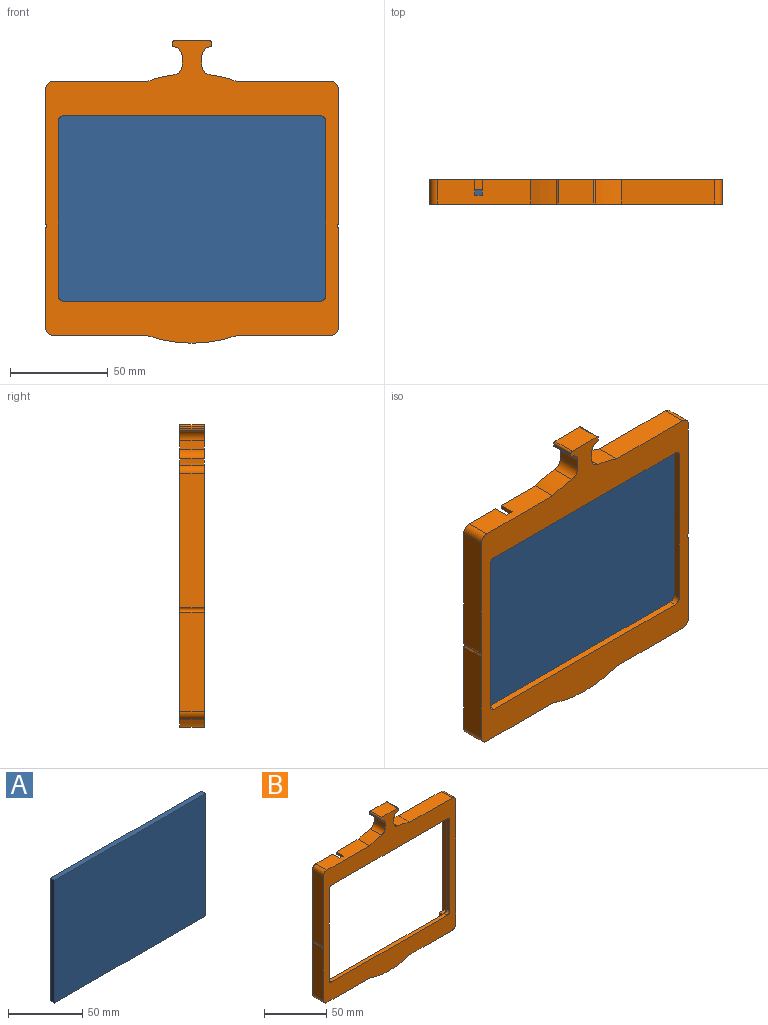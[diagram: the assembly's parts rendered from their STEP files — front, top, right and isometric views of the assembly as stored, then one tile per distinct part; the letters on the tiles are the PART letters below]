
ASSEMBLY  parts=2 mates=1
PART A: 6 faces, bbox 144x3.9x101.3 mm
  f0: plane 144x3.9mm, normal (0,0,1), area 561.6mm2, adj f1,f3,f4,f5
  f1: plane 101.3x3.9mm, normal (-1,0,0), area 395.1mm2, adj f0,f2,f4,f5
  f2: plane 144x3.9mm, normal (0,0,-1), area 561.6mm2, adj f1,f3,f4,f5
  f3: plane 101.3x3.9mm, normal (1,0,0), area 395.1mm2, adj f0,f2,f4,f5
  f4: plane 144x101.3mm, normal (0,-1,0), area 14587.2mm2, adj f0,f1,f2,f3
  f5: plane 144x101.3mm, normal (0,1,0), area 14587.2mm2, adj f0,f1,f2,f3
PART B: 106 faces, bbox 149.8x12.6x154.8 mm
  f0: plane 48.63x10mm, normal (0,0,1), area 486.3mm2, adj f1,f3,f51,f91,f95
  f1: plane 145.84x126mm, normal (0,1,0), area 3155mm2, adj f0,f2,f5,f6,f8,f10,f11,f50
  f2: plane 48.63x10mm, normal (0,0,-1), area 454.3mm2, adj f1,f3,f52,f85,f86,f87,f89,f94
  f3: plane 154.82x149.84mm, normal (0,1,0), area 1353.4mm2, adj f0,f2,f4,f5,f6,f7,f8,f9
  f4: plane 47.77x12.56mm, normal (0,0,1), area 568mm2, adj f3,f20,f33,f46,f85,f86,f87
  f5: plane 120x10mm, normal (-1,0,0), area 980.7mm2, adj f1,f3,f7,f9,f54,f55,f56,f58
  f6: plane 48.63x10mm, normal (0,0,1), area 430.3mm2, adj f1,f3,f7,f78,f80,f91,f96
  f7: cylinder r=3mm len=3mm, axis (0,-1,0), area 9.4mm2, adj f3,f5,f6,f78
  f8: plane 48.63x10mm, normal (0,0,-1), area 430.3mm2, adj f1,f3,f9,f71,f73,f89,f92
  f9: cylinder r=3mm len=3mm, axis (0,1,0), area 9.4mm2, adj f3,f5,f8,f71
  f10: plane 130.92x1mm, normal (0,0,1), area 130.9mm2, adj f1,f54,f57,f69
  f11: plane 130.92x1mm, normal (0,0,-1), area 130.9mm2, adj f1,f54,f61,f64
  f12: plane 131x3.56mm, normal (0,0,-1), area 466.4mm2, adj f16,f17,f20,f54
  f13: plane 89x3.56mm, normal (1,0,0), area 316.8mm2, adj f17,f18,f20,f54
  f14: plane 89x3.56mm, normal (-1,0,0), area 316.8mm2, adj f16,f19,f20,f54
  f15: plane 131x3.56mm, normal (0,0,1), area 466.4mm2, adj f18,f19,f20,f54
  f16: cylinder r=3mm len=3.56mm, axis (0,1,0), area 16.8mm2, adj f12,f14,f20,f54
  f17: cylinder r=3mm len=3.56mm, axis (0,-1,0), area 16.8mm2, adj f12,f13,f20,f54
  f18: cylinder r=3mm len=3.56mm, axis (0,1,0), area 16.8mm2, adj f13,f15,f20,f54
  f19: cylinder r=3mm len=3.56mm, axis (0,-1,0), area 16.8mm2, adj f14,f15,f20,f54
  f20: plane 154.82x149.84mm, normal (0,-1,0), area 6922mm2, adj f4,f12,f13,f14,f15,f16,f17,f18
  f21: plane 50.88x12.56mm, normal (-1,0,0), area 639.1mm2, adj f3,f20,f47,f49
  f22: plane 68.88x12.56mm, normal (1,0,0), area 865.2mm2, adj f3,f20,f45,f48
  f23: plane 50.88x12.56mm, normal (1,0,0), area 639.1mm2, adj f3,f20,f44,f48
  f24: plane 47.77x12.56mm, normal (0,0,1), area 600mm2, adj f3,f20,f25,f45
  f25: cylinder r=69mm len=13.83mm, axis (0,1,0), area 179.1mm2, adj f3,f20,f24,f42
  f26: plane 12.56x4.5mm, normal (1,0,0), area 56.5mm2, adj f3,f20,f27,f42
  f27: cylinder r=5mm len=12.56mm, axis (0,1,0), area 88.1mm2, adj f3,f20,f26,f38
  f28: plane 12.56x1.08mm, normal (1,0,0), area 13.6mm2, adj f3,f20,f38,f39
  f29: plane 18x12.56mm, normal (0,0,1), area 226.1mm2, adj f3,f20,f39,f40
  f30: plane 12.56x1.08mm, normal (-1,0,0), area 13.6mm2, adj f3,f20,f40,f41
  f31: cylinder r=5mm len=12.56mm, axis (0,1,0), area 88.1mm2, adj f3,f20,f32,f41
  f32: plane 12.56x4.5mm, normal (-1,0,0), area 56.5mm2, adj f3,f20,f31,f43
  f33: cylinder r=69mm len=13.83mm, axis (0,1,0), area 179.1mm2, adj f3,f4,f20,f43
  f34: plane 68.88x12.56mm, normal (-1,0,0), area 865.2mm2, adj f3,f20,f46,f49
  f35: plane 47.77x12.56mm, normal (0,0,-1), area 600mm2, adj f3,f20,f36,f47
  f36: cylinder r=69mm len=46.3mm, axis (0,1,0), area 593.1mm2, adj f3,f20,f35,f37
  f37: plane 47.77x12.56mm, normal (0,0,-1), area 600mm2, adj f3,f20,f36,f44
  f38: cylinder r=1mm len=12.56mm, axis (0,1,0), area 17.6mm2, adj f3,f20,f27,f28
  f39: cylinder r=1mm len=12.56mm, axis (0,1,0), area 19.7mm2, adj f3,f20,f28,f29
  f40: cylinder r=1mm len=12.56mm, axis (0,1,0), area 19.7mm2, adj f3,f20,f29,f30
  f41: cylinder r=1mm len=12.56mm, axis (0,1,0), area 17.6mm2, adj f3,f20,f30,f31
  f42: cylinder r=5mm len=12.56mm, axis (0,1,0), area 90.1mm2, adj f3,f20,f25,f26
  f43: cylinder r=5mm len=12.56mm, axis (0,1,0), area 90.1mm2, adj f3,f20,f32,f33
  f44: cylinder r=4mm len=12.56mm, axis (0,1,0), area 78.9mm2, adj f3,f20,f23,f37
  f45: cylinder r=4mm len=12.56mm, axis (0,1,0), area 78.9mm2, adj f3,f20,f22,f24
  f46: cylinder r=4mm len=12.56mm, axis (0,1,0), area 78.9mm2, adj f3,f4,f20,f34
  f47: cylinder r=4mm len=12.56mm, axis (0,1,0), area 78.9mm2, adj f3,f20,f21,f35
  f48: cylinder r=1.5mm len=12.56mm, axis (0,1,0), area 31.7mm2, adj f3,f20,f22,f23
  f49: cylinder r=1.5mm len=12.56mm, axis (0,1,0), area 31.7mm2, adj f3,f20,f21,f34
  f50: plane 120x10mm, normal (1,0,0), area 1200mm2, adj f1,f3,f51,f52
  f51: cylinder r=3mm len=10mm, axis (0,1,0), area 47.1mm2, adj f0,f1,f3,f50
  f52: cylinder r=3mm len=10mm, axis (0,-1,0), area 47.1mm2, adj f1,f2,f3,f50
  f53: plane 117.3x8mm, normal (-1,0,0), area 226.5mm2, adj f1,f54,f63,f66,f67,f70,f76,f84
  f54: plane 142.92x101.7mm, normal (0,1,0), area 1527.7mm2, adj f5,f10,f11,f12,f13,f14,f15,f16
  f55: plane 7x6mm, normal (0,0,-1), area 42mm2, adj f5,f54,f57,f58
  f56: plane 8x6mm, normal (0,0,1), area 48mm2, adj f1,f5,f57,f58
  f57: plane 8x3mm, normal (-1,0,0), area 24mm2, adj f1,f10,f55,f56,f58
  f58: plane 6x3mm, normal (0,1,0), area 18mm2, adj f5,f55,f56,f57
  f59: plane 7x6mm, normal (0,0,1), area 42mm2, adj f5,f54,f61,f62
  f60: plane 8x6mm, normal (0,0,-1), area 48mm2, adj f1,f5,f61,f62
  f61: plane 8x3mm, normal (-1,0,0), area 24mm2, adj f1,f11,f59,f60,f62
  f62: plane 6x3mm, normal (0,1,0), area 18mm2, adj f5,f59,f60,f61
  f63: plane 7x6mm, normal (0,0,1), area 42mm2, adj f53,f54,f64,f66
  f64: plane 8x3mm, normal (1,0,0), area 24mm2, adj f1,f11,f63,f65,f66
  f65: plane 8x4mm, normal (0,0,-1), area 32mm2, adj f1,f64,f66,f81
  f66: plane 7.8x6mm, normal (0,1,0), area 36.6mm2, adj f53,f63,f64,f65,f81,f82,f83,f84
  f67: plane 7x6mm, normal (0,0,-1), area 42mm2, adj f53,f54,f69,f70
  f68: plane 8x4mm, normal (0,0,1), area 32mm2, adj f1,f69,f70,f75
  f69: plane 8x3mm, normal (1,0,0), area 24mm2, adj f1,f10,f67,f68,f70
  f70: plane 7.8x6mm, normal (0,1,0), area 36.6mm2, adj f53,f67,f68,f69,f74,f75,f76,f77
  f71: plane 10x7.35mm, normal (0,1,0), area 66.7mm2, adj f5,f8,f9,f72,f73,f105
  f72: plane 10x8mm, normal (0,0,-1), area 80mm2, adj f1,f5,f71,f73
  f73: plane 8x7.35mm, normal (-1,0,0), area 58.8mm2, adj f1,f8,f71,f72
  f74: plane 8x3mm, normal (0,0,-1), area 24mm2, adj f1,f70,f75,f77
  f75: plane 8x1.8mm, normal (1,0,0), area 14.4mm2, adj f1,f68,f70,f74
  f76: plane 8x5mm, normal (0,0,1), area 40mm2, adj f1,f53,f70,f77
  f77: plane 8x3mm, normal (1,0,0), area 24mm2, adj f1,f70,f74,f76
  f78: plane 10x7.35mm, normal (0,1,0), area 66.7mm2, adj f5,f6,f7,f79,f80,f103
  f79: plane 10x8mm, normal (0,0,1), area 80mm2, adj f1,f5,f78,f80
  f80: plane 8x7.35mm, normal (-1,0,0), area 58.8mm2, adj f1,f6,f78,f79
  f81: plane 8x1.8mm, normal (1,0,0), area 14.4mm2, adj f1,f65,f66,f82
  f82: plane 8x3mm, normal (0,0,1), area 24mm2, adj f1,f66,f81,f83
  f83: plane 8x3mm, normal (1,0,0), area 24mm2, adj f1,f66,f82,f84
  f84: plane 8x5mm, normal (0,0,-1), area 40mm2, adj f1,f53,f66,f83
  f85: plane 8x2mm, normal (-1,0,0), area 16mm2, adj f2,f3,f4,f86
  f86: plane 4x2mm, normal (0,1,0), area 8mm2, adj f2,f4,f85,f87
  f87: plane 8x2mm, normal (1,0,0), area 16mm2, adj f2,f3,f4,f86
  f88: plane 42.58x8.5mm, normal (0,1,0), area 307.9mm2, adj f89,f92,f93,f94,f101
  f89: cylinder r=66.5mm len=42.58mm, axis (0,1,0), area 86.7mm2, adj f2,f3,f8,f88
  f90: plane 42.58x8.5mm, normal (0,1,0), area 307.9mm2, adj f91,f95,f96,f97,f99
  f91: cylinder r=66.5mm len=42.58mm, axis (0,1,0), area 86.7mm2, adj f0,f3,f6,f90
  f92: plane 8x5mm, normal (1,0,0), area 40mm2, adj f1,f8,f88,f93
  f93: plane 42.58x8mm, normal (0,0,-1), area 340.6mm2, adj f1,f88,f92,f94
  f94: plane 8x5mm, normal (-1,0,0), area 40mm2, adj f1,f2,f88,f93
  f95: plane 8x5mm, normal (-1,0,0), area 40mm2, adj f0,f1,f90,f97
  f96: plane 8x5mm, normal (1,0,0), area 40mm2, adj f1,f6,f90,f97
  f97: plane 42.58x8mm, normal (0,0,1), area 340.6mm2, adj f1,f90,f95,f96
  f98: cone r=0mm half-angle=59deg, axis (0,1,0), area 5.7mm2, adj f99
  f99: cylinder r=1.25mm len=6.5mm, axis (0,1,0), area 51.1mm2, adj f90,f98
  f100: cone r=0mm half-angle=59deg, axis (0,1,0), area 5.7mm2, adj f101
  f101: cylinder r=1.25mm len=6.5mm, axis (0,1,0), area 51.1mm2, adj f88,f100
  f102: cone r=0mm half-angle=59deg, axis (0,1,0), area 5.7mm2, adj f103
  f103: cylinder r=1.25mm len=6.5mm, axis (0,1,0), area 51.1mm2, adj f78,f102
  f104: cone r=0mm half-angle=59deg, axis (0,1,0), area 5.7mm2, adj f105
  f105: cylinder r=1.25mm len=6.5mm, axis (0,1,0), area 51.1mm2, adj f71,f104
PLACE A t=(-3.84,-2.7,0.1)mm
PLACE B t=(-4.76,2.4,0.1)mm
MATE fastened A.f3 <-> B.f5  axis (1,0,0) through (68.16,-6.6,0.1)mm
